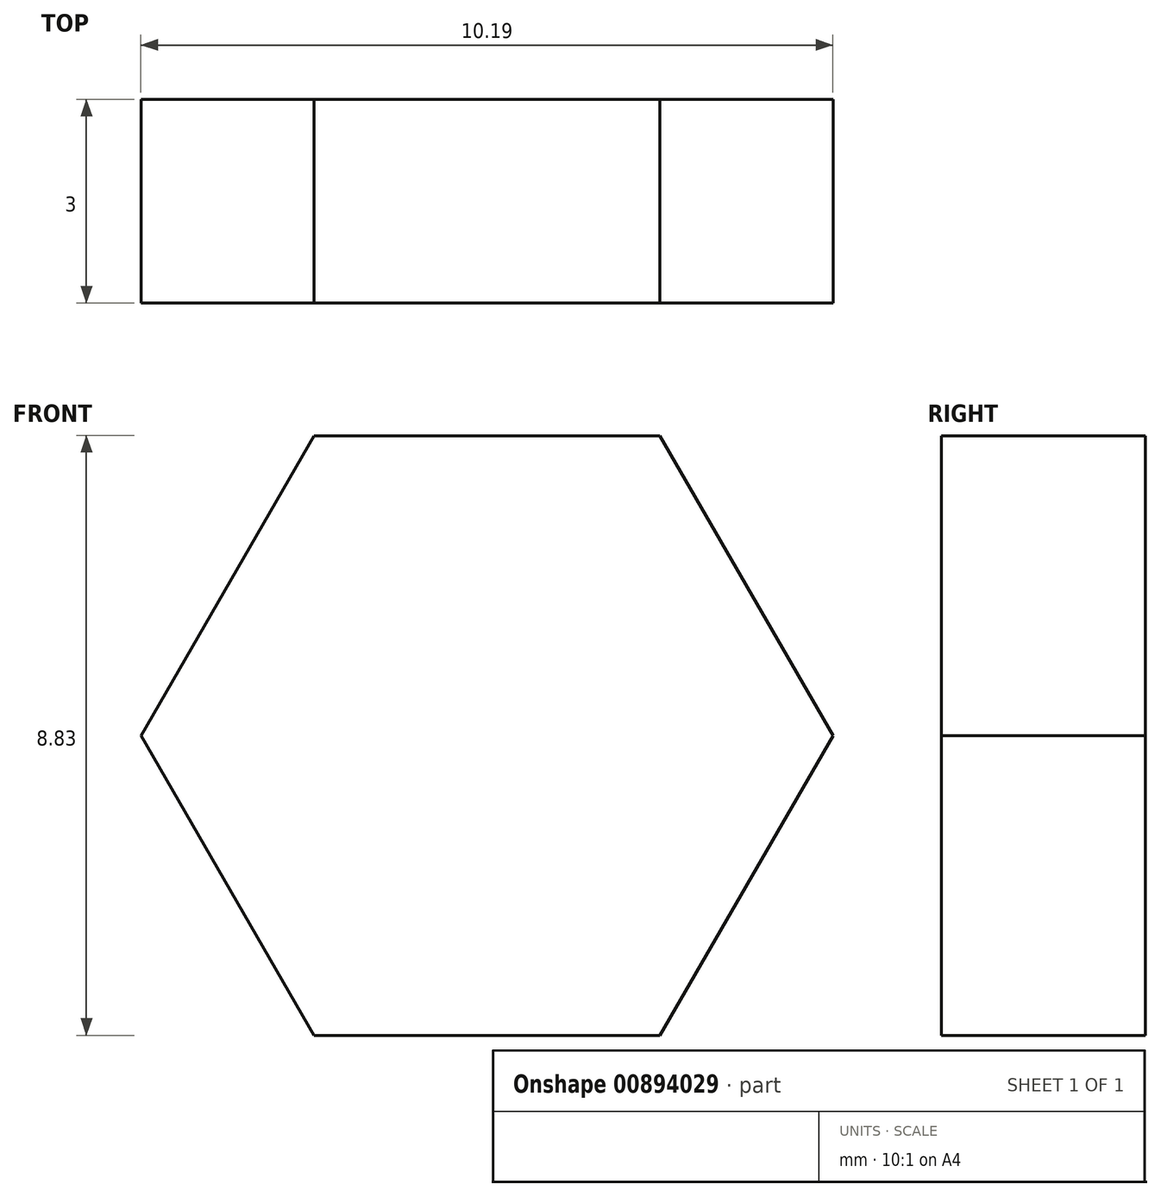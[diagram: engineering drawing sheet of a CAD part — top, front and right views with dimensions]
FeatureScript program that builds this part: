
annotation { "Feature Type Name" : "Feature", "Feature Type Description" : "" }
export const myFeature = defineFeature(function(context is Context, id is Id, definition is map)
    precondition{}
    {
        {
            var Q0;
            Q0=qCreatedBy(makeId("Front.planeOp"),FACE);
            var sketch = newSketch(context, id + "F0", { "sketchPlane" : qUnion([Q0])});
            skCircle(sketch, "E0.cCircle", {"center": v(-54.78, 14.66) * mm, "radius": 4.41 * mm, "construction": true});
            skLineSegment(sketch, "E0.0", {"start": v(-52.24, 10.25) * mm, "end": v(-57.33, 10.25) * mm});
            skLineSegment(sketch, "E0.1", {"start": v(-57.33, 10.25) * mm, "end": v(-59.88, 14.66) * mm});
            skLineSegment(sketch, "E0.2", {"start": v(-59.88, 14.66) * mm, "end": v(-57.33, 19.08) * mm});
            skLineSegment(sketch, "E0.3", {"start": v(-57.33, 19.08) * mm, "end": v(-52.24, 19.08) * mm});
            skLineSegment(sketch, "E0.4", {"start": v(-52.24, 19.08) * mm, "end": v(-49.69, 14.66) * mm});
            skLineSegment(sketch, "E0.5", {"start": v(-49.69, 14.66) * mm, "end": v(-52.24, 10.25) * mm});
            skPoint(sketch, "E0.0.midPoint", {"position": v(-54.78, 10.25) * mm});
            skSolve(sketch);
        }
        {
            var Q0;
            Q0=makeQuery(id+"F0.imprint","IMPRINT",FACE,{"disambiguationData":[TD([[makeQuery(id+"F0.imprint","IMPRINT",EDGE,{"derivedFrom":sQuery(id+"F0.wireOp",EDGE,"E0.0")}),-1.0]])]});
            extrude(context, id + "F1", {"entities" : qUnion([Q0]), "depth" : 3 * mm, "offsetDistance" : 25 * mm});
        }
    });
